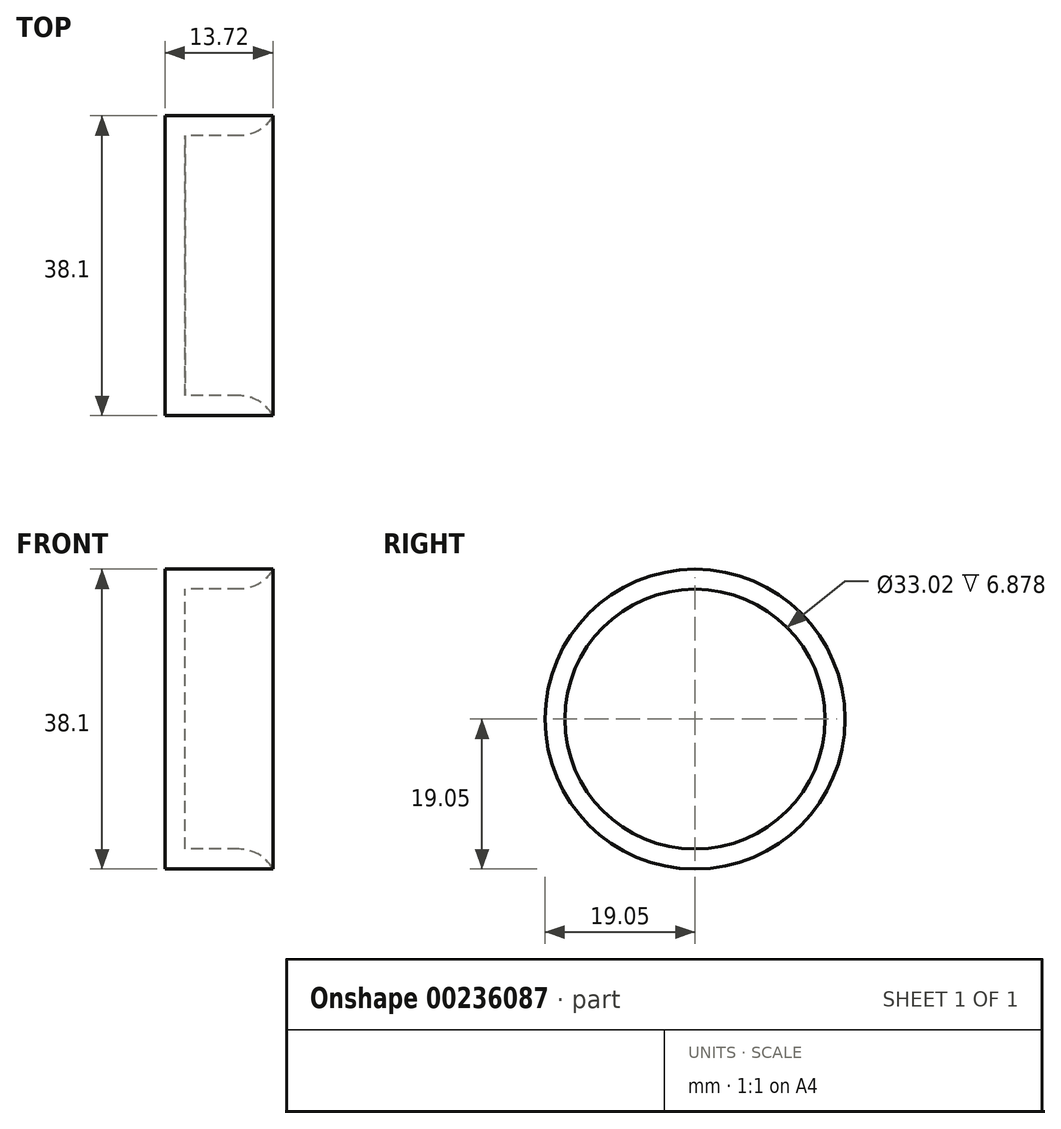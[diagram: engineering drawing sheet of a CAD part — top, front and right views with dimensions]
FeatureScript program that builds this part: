
annotation { "Feature Type Name" : "Feature", "Feature Type Description" : "" }
export const myFeature = defineFeature(function(context is Context, id is Id, definition is map)
    precondition{}
    {
        {
            var Q0;
            Q0=qCreatedBy(makeId("Right.planeOp"),FACE);
            var sketch = newSketch(context, id + "F0", { "sketchPlane" : qUnion([Q0])});
            skCircle(sketch, "E0", {"center": v(0, 0) * mm, "radius": 6.35 * mm});
            skCircle(sketch, "E1", {"center": v(0, 0) * mm, "radius": 19.05 * mm});
            skCircle(sketch, "E2", {"center": v(0, 0) * mm, "radius": 12.7 * mm});
            skSolve(sketch);
        }
        {
            var Q0;
            Q0=makeQuery(id+"F0.imprint","IMPRINT",FACE,{"disambiguationData":[TD([[makeQuery(id+"F0.imprint","IMPRINT",EDGE,{"derivedFrom":sQuery(id+"F0.wireOp",EDGE,"E0")}),1.0]])]});
            var Q1;
            Q1=makeQuery(id+"F0.imprint","IMPRINT",FACE,{"disambiguationData":[TD([[makeQuery(id+"F0.imprint","IMPRINT",EDGE,{"derivedFrom":sQuery(id+"F0.wireOp",EDGE,"E0")}),-1.0]])]});
            var Q2;
            Q2=makeQuery(id+"F0.imprint","IMPRINT",FACE,{"disambiguationData":[TD([[makeQuery(id+"F0.imprint","IMPRINT",EDGE,{"derivedFrom":sQuery(id+"F0.wireOp",EDGE,"E1")}),1.0]])]});
            extrude(context, id + "F1", {"entities" : qUnion([Q0, Q1, Q2]), "endBound" : BoundingType.SYMMETRIC, "depth" : 13.72 * mm});
        }
        {
            var Q0;
            Q0=makeQuery(id+"F1.opExtrude","CAP_FACE",FACE,{"disambiguationData":[OSD([sQuery(id+"F0.wireOp",EDGE,"E1")])],"isStart":false});
            shell(context, id + "F2", {"entities" : qUnion([Q0]), "thickness" : 2.54 * mm});
        }
        {
            var Q0;
            Q0=sQuery(id+"F0.wireOp",EDGE,"E2");
            extrude(context, id + "F3", {"bodyType" : ToolBodyType.SURFACE, "surfaceEntities" : qUnion([Q0]), "depth" : 4.06 * mm});
        }
        {
            var Q0;
            {var subQ0=sQuery(id+"F0.wireOp",EDGE,"E1");Q0=makeQuery(id+"F2.opShell","OFFSET_EDGE",EDGE,{"disambiguationData":[OSD([subQ0]),TDD([makeQuery(id+"F1.opExtrude","CAP_EDGE",EDGE,{"disambiguationData":[OSD([subQ0])],"isStart":false})])]});}
            fillet(context, id + "F4", {"entities" : qUnion([Q0]), "radius" : 4.9 * mm, "tangentPropagation" : true, "allowEdgeOverflow" : false});
        }
    });
